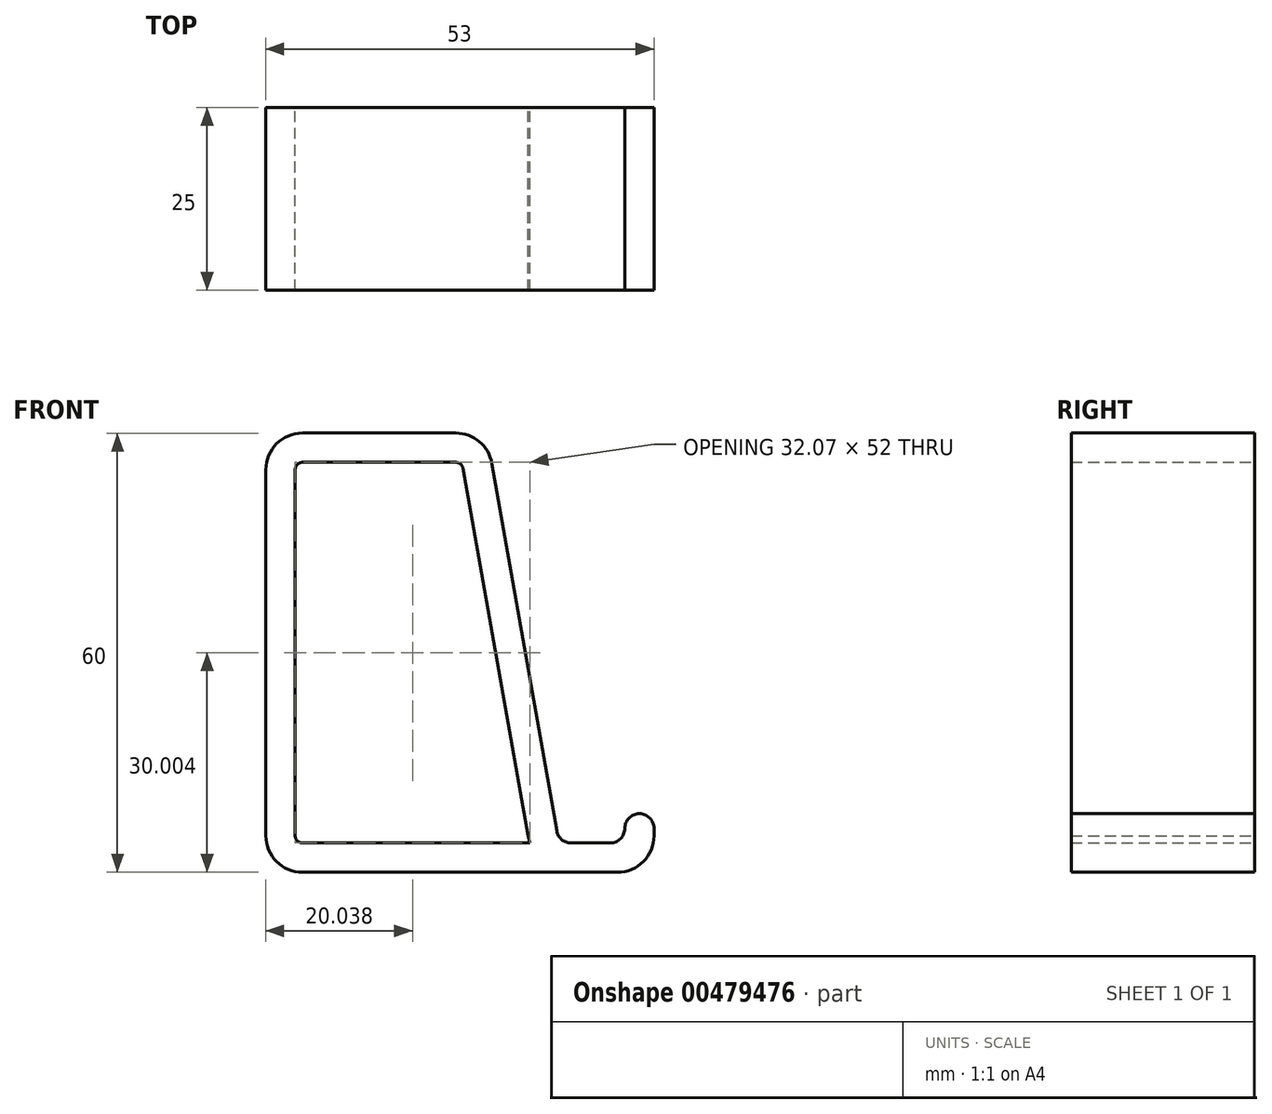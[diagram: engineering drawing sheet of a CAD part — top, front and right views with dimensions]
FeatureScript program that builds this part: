
annotation { "Feature Type Name" : "Feature", "Feature Type Description" : "" }
export const myFeature = defineFeature(function(context is Context, id is Id, definition is map)
    precondition{}
    {
        {
            var Q0;
            Q0=qCreatedBy(makeId("Front.planeOp"),FACE);
            var sketch = newSketch(context, id + "F0", { "sketchPlane" : qUnion([Q0])});
            skLineSegment(sketch, "E0", {"start": v(-61.52, -168.95) * mm, "end": v(-18.52, -168.95) * mm});
            skLineSegment(sketch, "E1", {"start": v(-13.52, -163.95) * mm, "end": v(-13.52, -162.95) * mm});
            skLineSegment(sketch, "E2", {"start": v(-15.52, -160.95) * mm, "end": v(-15.52, -160.95) * mm});
            skLineSegment(sketch, "E3", {"start": v(-17.52, -162.95) * mm, "end": v(-17.52, -162.95) * mm});
            skLineSegment(sketch, "E4", {"start": v(-19.52, -164.95) * mm, "end": v(-24.84, -164.95) * mm});
            skLineSegment(sketch, "E5", {"start": v(-26.8, -163.3) * mm, "end": v(-35.66, -113.08) * mm});
            skLineSegment(sketch, "E6", {"start": v(-66.52, -113.95) * mm, "end": v(-66.52, -163.95) * mm});
            skLineSegment(sketch, "E7", {"start": v(-61.52, -108.95) * mm, "end": v(-40.59, -108.95) * mm});
            skPoint(sketch, "E8.visualSharp", {"position": v(-36.4, -108.95) * mm});
            skArc(sketch, "E8.filletArc", {"start": v(-35.66, -113.08) * mm, "mid": v(-37.37, -110.12) * mm, "end": v(-40.59, -108.95) * mm});
            skPoint(sketch, "E9.visualSharp", {"position": v(-66.52, -108.95) * mm});
            skArc(sketch, "E9.filletArc", {"start": v(-61.52, -108.95) * mm, "mid": v(-65.05, -110.41) * mm, "end": v(-66.52, -113.95) * mm});
            skPoint(sketch, "E10.visualSharp", {"position": v(-66.52, -168.95) * mm});
            skArc(sketch, "E10.filletArc", {"start": v(-66.52, -163.95) * mm, "mid": v(-65.05, -167.48) * mm, "end": v(-61.52, -168.95) * mm});
            skPoint(sketch, "E11.visualSharp", {"position": v(-13.52, -168.95) * mm});
            skArc(sketch, "E11.filletArc", {"start": v(-18.52, -168.95) * mm, "mid": v(-14.98, -167.48) * mm, "end": v(-13.52, -163.95) * mm});
            skPoint(sketch, "E12.visualSharp", {"position": v(-13.52, -160.95) * mm});
            skArc(sketch, "E12.filletArc", {"start": v(-13.52, -162.95) * mm, "mid": v(-14.1, -161.53) * mm, "end": v(-15.52, -160.95) * mm});
            skPoint(sketch, "E13.visualSharp", {"position": v(-17.52, -160.95) * mm});
            skArc(sketch, "E13.filletArc", {"start": v(-15.52, -160.95) * mm, "mid": v(-16.93, -161.53) * mm, "end": v(-17.52, -162.95) * mm});
            skPoint(sketch, "E14.visualSharp", {"position": v(-17.52, -164.95) * mm});
            skArc(sketch, "E14.filletArc", {"start": v(-19.52, -164.95) * mm, "mid": v(-18.1, -164.36) * mm, "end": v(-17.52, -162.95) * mm});
            skPoint(sketch, "E15.visualSharp", {"position": v(-26.52, -164.95) * mm});
            skArc(sketch, "E15.filletArc", {"start": v(-26.8, -163.3) * mm, "mid": v(-26.12, -164.48) * mm, "end": v(-24.84, -164.95) * mm});
            skLineSegment(sketch, "E16.0", {"start": v(-30.75, -163.99) * mm, "end": v(-39.6, -113.77) * mm});
            skArc(sketch, "E16.1", {"start": v(-39.6, -113.77) * mm, "mid": v(-39.94, -113.18) * mm, "end": v(-40.59, -112.95) * mm});
            skLineSegment(sketch, "E16.2", {"start": v(-61.52, -112.95) * mm, "end": v(-40.59, -112.95) * mm});
            skLineSegment(sketch, "E16.3", {"start": v(-26.52, -164.95) * mm, "end": v(-18.52, -164.95) * mm});
            skArc(sketch, "E16.4", {"start": v(-62.52, -163.95) * mm, "mid": v(-62.22, -164.65) * mm, "end": v(-61.52, -164.95) * mm});
            skLineSegment(sketch, "E16.5", {"start": v(-62.52, -113.95) * mm, "end": v(-62.52, -163.95) * mm});
            skArc(sketch, "E16.6", {"start": v(-61.52, -112.95) * mm, "mid": v(-62.22, -113.24) * mm, "end": v(-62.52, -113.95) * mm});
            skLineSegment(sketch, "E17", {"start": v(-61.52, -164.95) * mm, "end": v(-30.45, -164.95) * mm});
            skLineSegment(sketch, "E18", {"start": v(-30.45, -164.95) * mm, "end": v(-30.75, -163.99) * mm});
            skSolve(sketch);
        }
        {
            var Q0;
            Q0=makeQuery(id+"F0.imprint","IMPRINT",FACE,{"disambiguationData":[TD([[makeQuery(id+"F0.imprint","IMPRINT",EDGE,{"derivedFrom":sQuery(id+"F0.wireOp",EDGE,"E0")}),1.0]])]});
            extrude(context, id + "F1", {"entities" : qUnion([Q0]), "depth" : 25 * mm});
        }
    });
